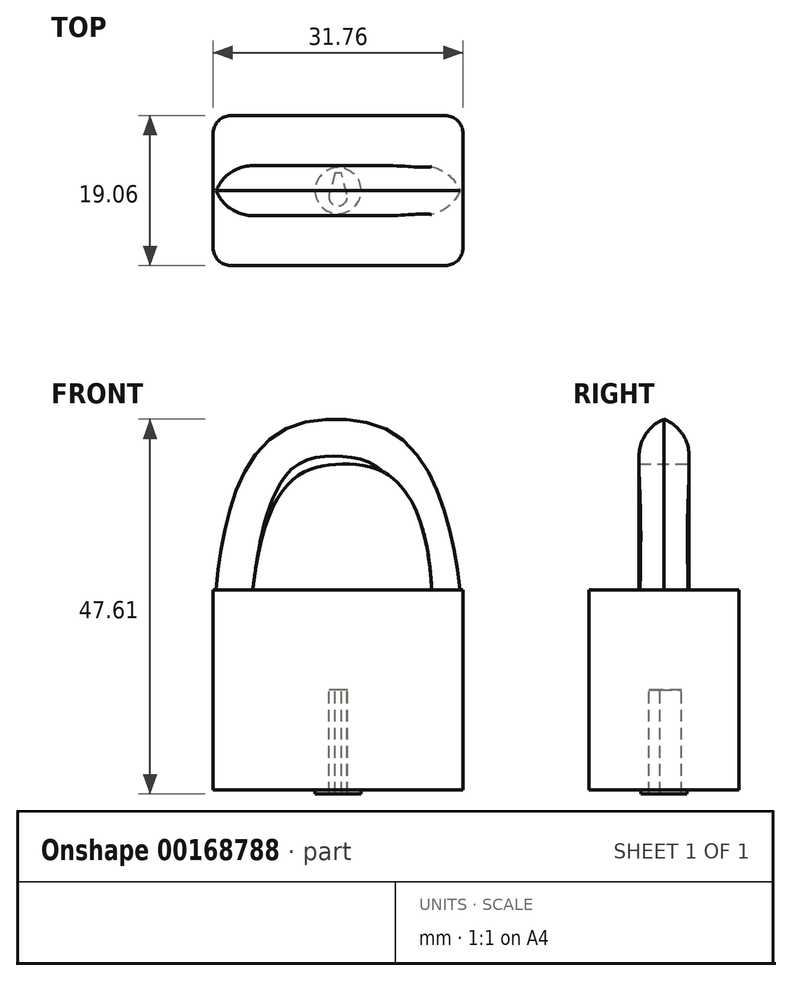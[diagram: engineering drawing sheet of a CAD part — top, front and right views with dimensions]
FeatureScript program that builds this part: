
annotation { "Feature Type Name" : "Feature", "Feature Type Description" : "" }
export const myFeature = defineFeature(function(context is Context, id is Id, definition is map)
    precondition{}
    {
        {
            var Q0;
            Q0=qCreatedBy(makeId("Front.planeOp"),FACE);
            var sketch = newSketch(context, id + "F0", { "sketchPlane" : qUnion([Q0])});
            skLineSegment(sketch, "E0.bottom", {"start": v(15.88, 12.7) * mm, "end": v(-15.88, 12.7) * mm});
            skLineSegment(sketch, "E0.top", {"start": v(15.87, -12.7) * mm, "end": v(-15.88, -12.7) * mm});
            skLineSegment(sketch, "E0.left", {"start": v(15.87, 12.7) * mm, "end": v(15.88, -12.7) * mm});
            skLineSegment(sketch, "E0.right", {"start": v(-15.88, 12.7) * mm, "end": v(-15.87, -12.7) * mm});
            skPoint(sketch, "E0.middle", {"position": v(0, 0) * mm});
            skFitSpline(sketch, "E1", {"points": [v(-15.88, 12.7) * mm, v(0, 34.76) * mm, v(15.87, 12.7) * mm], "startDerivative": vector(10.65, 119.46) * mm, "endDerivative": vector(14.15, -115.9) * mm});
            skFitSpline(sketch, "E2", {"points": [v(-10.83, 12.7) * mm, v(0, 28.7) * mm, v(11.89, 12.7) * mm], "startDerivative": vector(9.33, 82.3) * mm, "endDerivative": vector(4.73, -87.29) * mm});
            skFitSpline(sketch, "E3", {"points": [v(-13.87, -12.7) * mm, v(-11.7, -15.98) * mm, v(-9.54, -12.7) * mm], "startDerivative": vector(-0.23, -19.8) * mm, "endDerivative": vector(0, 19.7) * mm});
            skFitSpline(sketch, "E4", {"points": [v(13.87, -12.7) * mm, v(11.7, -15.98) * mm, v(9.54, -12.7) * mm], "startDerivative": vector(2.91, -19.7) * mm, "endDerivative": vector(-0.9, 21.77) * mm});
            skSolve(sketch);
        }
        {
            var Q0;
            Q0=makeQuery(id+"F0.imprint","IMPRINT",FACE,{"disambiguationData":[TD([[makeQuery(id+"F0.imprint","IMPRINT",EDGE,{"derivedFrom":sQuery(id+"F0.wireOp",EDGE,"E0.top")}),-1.0]])]});
            extrude(context, id + "F1", {"entities" : qUnion([Q0]), "endBound" : BoundingType.SYMMETRIC, "depth" : 19.05 * mm});
        }
        {
            var Q0;
            {var subQ0=sQuery(id+"F0.wireOp",EDGE,"E1");Q0=makeQuery(id+"F0.imprint","IMPRINT",FACE,{"disambiguationData":[TD([[makeQuery(id+"F0.imprint","IMPRINT",EDGE,{"derivedFrom":subQ0}),-1.0]])]});}
            extrude(context, id + "F2", {"entities" : qUnion([Q0]), "operationType" : NewBodyOperationType.ADD, "endBound" : BoundingType.SYMMETRIC, "depth" : 6.35 * mm});
        }
        {
            var Q0;
            Q0=makeQuery(id+"F2.opExtrude","CAP_EDGE",EDGE,{"disambiguationData":[OSD([sQuery(id+"F0.wireOp",EDGE,"E1")])],"isStart":false});
            fillet(context, id + "F3", {"entities" : qUnion([Q0]), "radius" : 5.08 * mm, "tangentPropagation" : true, "allowEdgeOverflow" : false});
        }
        {
            var Q0;
            Q0=makeQuery(id+"F2.opExtrude","CAP_EDGE",EDGE,{"disambiguationData":[OSD([sQuery(id+"F0.wireOp",EDGE,"E1")])],"isStart":true});
            fillet(context, id + "F4", {"entities" : qUnion([Q0]), "radius" : 5.08 * mm, "tangentPropagation" : true, "allowEdgeOverflow" : false});
        }
        {
            var Q0;
            Q0=makeQuery(id+"F1.opExtrude","CAP_EDGE",EDGE,{"disambiguationData":[OSD([sQuery(id+"F0.wireOp",EDGE,"E0.left")])],"isStart":false});
            fillet(context, id + "F5", {"entities" : qUnion([Q0]), "radius" : 2.3 * mm, "tangentPropagation" : true, "allowEdgeOverflow" : false});
        }
        {
            var Q0;
            Q0=makeQuery(id+"F1.opExtrude","CAP_EDGE",EDGE,{"disambiguationData":[OSD([sQuery(id+"F0.wireOp",EDGE,"E0.right")])],"isStart":false});
            var Q1;
            Q1=makeQuery(id+"F1.opExtrude","CAP_EDGE",EDGE,{"disambiguationData":[OSD([sQuery(id+"F0.wireOp",EDGE,"E0.right")])],"isStart":true});
            var Q2;
            Q2=makeQuery(id+"F1.opExtrude","CAP_EDGE",EDGE,{"disambiguationData":[OSD([sQuery(id+"F0.wireOp",EDGE,"E0.left")])],"isStart":true});
            fillet(context, id + "F6", {"entities" : qUnion([Q0, Q1, Q2]), "radius" : 2.3 * mm, "tangentPropagation" : true, "allowEdgeOverflow" : false});
        }
        {
            var Q0;
            Q0=makeQuery(id+"F1.opExtrude","SWEPT_FACE",FACE,{"disambiguationData":[OSD([sQuery(id+"F0.wireOp",EDGE,"E0.top")])]});
            var sketch = newSketch(context, id + "F7", { "sketchPlane" : qUnion([Q0])});
            skCircle(sketch, "E5", {"center": v(0, 0) * mm, "radius": 2.92 * mm});
            skArc(sketch, "E6", {"start": v(1.15, 0.52) * mm, "mid": v(-0.03, 1.94) * mm, "end": v(-1.14, 0.46) * mm});
            skLineSegment(sketch, "E7", {"start": v(-1.14, 0.46) * mm, "end": v(-0.4, -2.23) * mm});
            skLineSegment(sketch, "E8", {"start": v(-0.4, -2.23) * mm, "end": v(0.4, -2.23) * mm});
            skLineSegment(sketch, "E9", {"start": v(0.4, -2.23) * mm, "end": v(1.15, 0.52) * mm});
            skSolve(sketch);
        }
        {
            var Q0;
            Q0 = qSketchRegion(id + "F7", true);
            extrude(context, id + "F8", {"entities" : qUnion([Q0]), "operationType" : NewBodyOperationType.ADD, "endBound" : BoundingType.SYMMETRIC, "depth" : 1.02 * mm});
        }
        {
            var Q0;
            Q0=makeQuery(id+"F8.boolean.opBoolean","SPLIT",FACE,{"disambiguationData":[TD([makeQuery(id+"F8.opExtrude","SWEPT_FACE",FACE,{"disambiguationData":[OSD([sQuery(id+"F7.wireOp",EDGE,"E6")])]})])],"derivedFrom":makeQuery(id+"F1.opExtrude","SWEPT_FACE",FACE,{"disambiguationData":[OSD([sQuery(id+"F0.wireOp",EDGE,"E0.top")])]})});
            extrude(context, id + "F9", {"entities" : qUnion([Q0]), "operationType" : NewBodyOperationType.REMOVE, "oppositeDirection" : true, "depth" : 12.7 * mm});
        }
    });
